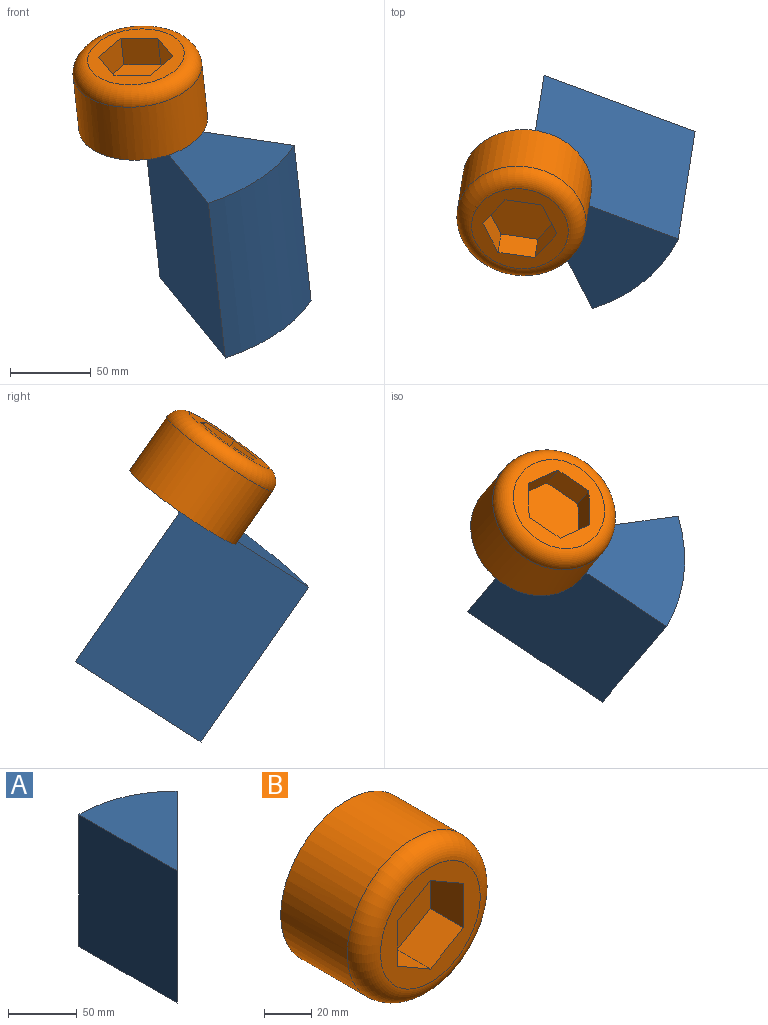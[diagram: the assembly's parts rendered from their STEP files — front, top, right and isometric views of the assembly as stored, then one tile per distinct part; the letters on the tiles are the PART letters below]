
ASSEMBLY  parts=2 mates=3
PART A: 5 faces, bbox 71.1x100.6x117.1 mm
  f0: plane 100.6x71.13mm, normal (0,0,-1), area 3973.9mm2, adj f1,f3,f4
  f1: cylinder r=100.6mm len=117.06mm, axis (0,0,1), area 9248.3mm2, adj f0,f2,f3,f4
  f2: plane 100.6x71.13mm, normal (0,0,1), area 3973.9mm2, adj f1,f3,f4
  f3: plane 117.06x71.13mm, normal (0.71,-0.71,0), area 11775.3mm2, adj f0,f1,f2,f4
  f4: plane 117.06x100.6mm, normal (-1,0,0), area 11775.3mm2, adj f0,f1,f2,f3
PART B: 21 faces, bbox 86.6x50x86.6 mm
  f0: plane 60x60mm, normal (0,-1,0), area 1441.8mm2, adj f3,f4,f5,f6,f7,f8,f10
  f1: cylinder r=40mm len=80mm, axis (0,1,0), area 10053.1mm2, adj f2,f10
  f2: plane 80x80mm, normal (0,1,0), area 608.7mm2, adj f1,f12
  f3: plane 20x20mm, normal (0.5,0,-0.87), area 461.9mm2, adj f0,f4,f8,f9
  f4: plane 23.09x20mm, normal (1,0,0), area 461.9mm2, adj f0,f3,f5,f9
  f5: plane 20x20mm, normal (0.5,0,0.87), area 461.9mm2, adj f0,f4,f6,f9
  f6: plane 20x20mm, normal (-0.5,0,0.87), area 461.9mm2, adj f0,f5,f7,f9
  f7: plane 23.09x20mm, normal (-1,0,0), area 461.9mm2, adj f0,f6,f8,f9
  f8: plane 20x20mm, normal (-0.5,0,-0.87), area 461.9mm2, adj f0,f3,f7,f9
  f9: plane 46.19x40mm, normal (0,-1,0), area 1385.6mm2, adj f3,f4,f5,f6,f7,f8
  f10: torus R=30mm, axis (0,-1,0), area 3589.2mm2, adj f0,f1
  f11: plane 60x60mm, normal (0,1,0), area 1073.7mm2, adj f13,f14,f15,f16,f17,f18,f20
  f12: cylinder r=37.5mm len=75mm, axis (0,1,0), area 9424.8mm2, adj f2,f20
  f13: plane 22.5x20mm, normal (-0.5,0,0.87), area 519.6mm2, adj f11,f14,f18,f19
  f14: plane 25.98x20mm, normal (-1,0,0), area 519.6mm2, adj f11,f13,f15,f19
  f15: plane 22.5x20mm, normal (-0.5,0,-0.87), area 519.6mm2, adj f11,f14,f16,f19
  f16: plane 22.5x20mm, normal (0.5,0,-0.87), area 519.6mm2, adj f11,f15,f17,f19
  f17: plane 25.98x20mm, normal (1,0,0), area 519.6mm2, adj f11,f16,f18,f19
  f18: plane 22.5x20mm, normal (0.5,0,0.87), area 519.6mm2, adj f11,f13,f17,f19
  f19: plane 51.96x45mm, normal (0,1,0), area 1753.7mm2, adj f13,f14,f15,f16,f17,f18
  f20: torus R=30mm, axis (0,-1,0), area 2574.1mm2, adj f11,f12
PLACE A rot(axis=(-0.98,-0.19,-0.11),147deg) t=(-182.57,272.64,-135.07)mm
PLACE B rot(axis=(-0.91,-0.4,0.11),60.9deg) t=(-198.86,242.02,-55.78)mm
MATE cylindrical A.f1 <-> B.f1  axis (0.09,0.57,-0.82) through (-193.63,275.29,-103.64)mm
MATE planar A.f0 <-> B.f1  axis (-0.09,-0.57,0.82) through (-151.86,202.49,-78.12)mm
MATE slider A.f1 <-> B.f1  axis (0.09,0.57,-0.82) through (-193.63,275.29,-103.64)mm
